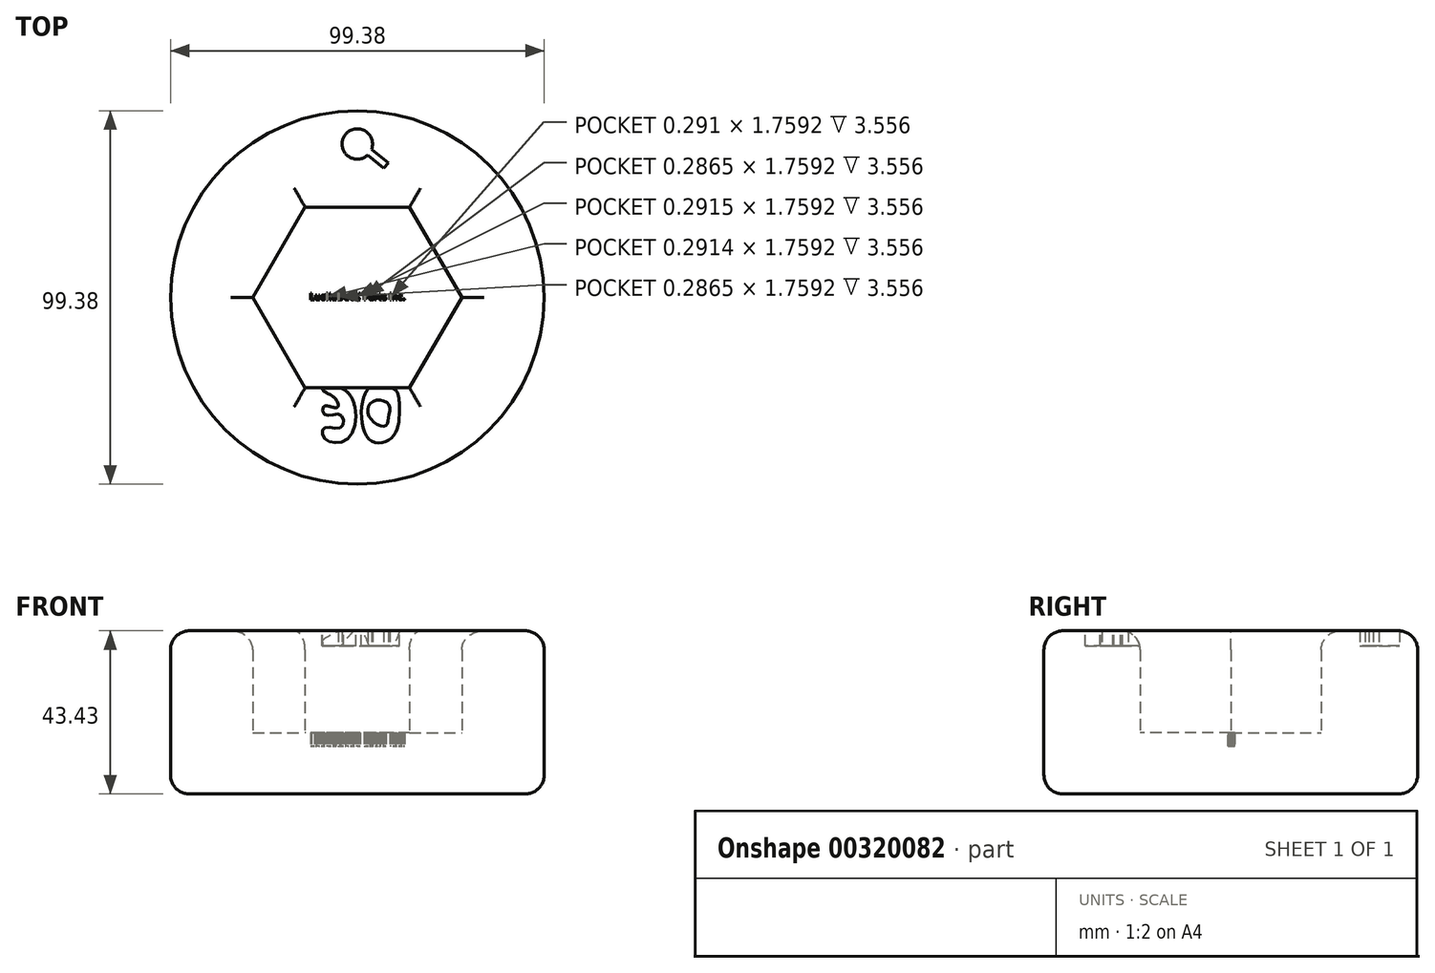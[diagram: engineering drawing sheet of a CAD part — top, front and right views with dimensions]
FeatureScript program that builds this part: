
annotation { "Feature Type Name" : "Feature", "Feature Type Description" : "" }
export const myFeature = defineFeature(function(context is Context, id is Id, definition is map)
    precondition{}
    {
        {
            var Q0;
            Q0=qCreatedBy(makeId("Top.planeOp"),FACE);
            var sketch = newSketch(context, id + "F0", { "sketchPlane" : qUnion([Q0])});
            skCircle(sketch, "E0", {"center": v(0, 0) * mm, "radius": 49.69 * mm});
            skCircle(sketch, "E1.cCircle", {"center": v(0, 0) * mm, "radius": 24.06 * mm, "construction": true});
            skLineSegment(sketch, "E1.0", {"start": v(-13.9, 24.06) * mm, "end": v(13.9, 24.06) * mm});
            skLineSegment(sketch, "E1.1", {"start": v(13.9, 24.06) * mm, "end": v(27.78, 0) * mm});
            skLineSegment(sketch, "E1.2", {"start": v(27.78, 0) * mm, "end": v(13.9, -24.06) * mm});
            skLineSegment(sketch, "E1.3", {"start": v(13.9, -24.06) * mm, "end": v(-13.9, -24.06) * mm});
            skLineSegment(sketch, "E1.4", {"start": v(-13.9, -24.06) * mm, "end": v(-27.78, 0) * mm});
            skLineSegment(sketch, "E1.5", {"start": v(-27.78, 0) * mm, "end": v(-13.9, 24.06) * mm});
            skPoint(sketch, "E1.0.midPoint", {"position": v(0, 24.06) * mm});
            skPoint(sketch, "E2.oppositeSnap0", {"position": v(0, -24.06) * mm});
            skSolve(sketch);
        }
        {
            var Q0;
            Q0=makeQuery(id+"F0.imprint","IMPRINT",FACE,{"disambiguationData":[TD([[makeQuery(id+"F0.imprint","IMPRINT",EDGE,{"derivedFrom":sQuery(id+"F0.wireOp",EDGE,"E0")}),1.0]])]});
            extrude(context, id + "F1", {"entities" : qUnion([Q0]), "depth" : 43.43 * mm});
        }
        {
            var Q0;
            Q0=qCreatedBy(makeId("Top.planeOp"),FACE);
            var sketch = newSketch(context, id + "F2", { "sketchPlane" : qUnion([Q0])});
            skCircle(sketch, "E3.cCircle", {"center": v(0, 0) * mm, "radius": 32.73 * mm, "construction": true});
            skLineSegment(sketch, "E3.0", {"start": v(18.9, -32.73) * mm, "end": v(-18.9, -32.73) * mm});
            skLineSegment(sketch, "E3.1", {"start": v(-18.9, -32.73) * mm, "end": v(-37.8, 0) * mm});
            skLineSegment(sketch, "E3.2", {"start": v(-37.8, 0) * mm, "end": v(-18.9, 32.73) * mm});
            skLineSegment(sketch, "E3.3", {"start": v(-18.9, 32.73) * mm, "end": v(18.9, 32.73) * mm});
            skLineSegment(sketch, "E3.4", {"start": v(18.9, 32.73) * mm, "end": v(37.8, 0) * mm});
            skLineSegment(sketch, "E3.5", {"start": v(37.8, 0) * mm, "end": v(18.9, -32.73) * mm});
            skPoint(sketch, "E3.0.midPoint", {"position": v(0, -32.73) * mm});
            skSolve(sketch);
        }
        {
            var Q0;
            Q0 = qSketchRegion(id + "F2", true);
            extrude(context, id + "F3", {"entities" : qUnion([Q0]), "operationType" : NewBodyOperationType.ADD, "depth" : 16.26 * mm});
        }
        {
            var Q0;
            Q0=qCreatedBy(makeId("Top.planeOp"),FACE);
            cPlane(context, id + "F4", {"entities" : qUnion([Q0]), "cplaneType" : CPlaneType.OFFSET, "offset" : 12.7 * mm, "width" : 152.4 * mm, "height" : 152.4 * mm});
        }
        {
            var Q0;
            Q0=qCreatedBy(id+"F4.planeOp",FACE);
            var sketch = newSketch(context, id + "F5", { "sketchPlane" : qUnion([Q0])});
            skText(sketch, "E4", { "text": "LucKaDucK Parts Inc.", "fontName": "AllertaStencil-Regular.ttf"});
            const initialGuessF5  = {"E4": [-0.0127, -0.00066, 1, 0, 0.00176]};
            skSetInitialGuess(sketch, initialGuessF5);
            skSolve(sketch);
        }
        {
            var Q0;
            Q0 = qSketchRegion(id + "F5", true);
            extrude(context, id + "F6", {"entities" : qUnion([Q0]), "operationType" : NewBodyOperationType.REMOVE, "depth" : 4.6 * mm});
        }
        {
            var Q0;
            Q0=qCreatedBy(makeId("Top.planeOp"),FACE);
            cPlane(context, id + "F7", {"entities" : qUnion([Q0]), "cplaneType" : CPlaneType.OFFSET, "offset" : 39.37 * mm, "width" : 152.4 * mm, "height" : 152.4 * mm});
        }
        {
            var Q0;
            Q0=qCreatedBy(id+"F7.planeOp",FACE);
            var sketch = newSketch(context, id + "F8", { "sketchPlane" : qUnion([Q0])});
            skFitSpline(sketch, "E5", {"points": [v(-9.26, -24.46) * mm, v(-3.12, -24.78) * mm, v(-1.98, -37) * mm, v(-8.58, -37.65) * mm, v(-8.8, -34.76) * mm, v(-4.26, -34.44) * mm, v(-4.49, -31.22) * mm, v(-8.58, -31.22) * mm, v(-8.8, -28.97) * mm, v(-5.4, -29.29) * mm, v(-6.08, -26.71) * mm, v(-9.26, -24.46) * mm]});
            skFitSpline(sketch, "E6", {"points": [v(2.8, -24.46) * mm, v(2.8, -37.33) * mm, v(9.16, -37.33) * mm, v(11.2, -29.29) * mm, v(10.3, -24.78) * mm, v(7.8, -23.82) * mm, v(2.8, -24.46) * mm]});
            skFitSpline(sketch, "E7", {"points": [v(5.07, -27.36) * mm, v(2.8, -29.6) * mm, v(4.38, -33.15) * mm, v(7.57, -34.11) * mm, v(8.25, -31.86) * mm, v(8.48, -28.64) * mm, v(5.07, -27.36) * mm]});
            skCircle(sketch, "E8", {"center": v(0, 40.84) * mm, "radius": 4.05 * mm});
            skLineSegment(sketch, "E9", {"start": v(2.79, 37.9) * mm, "end": v(7.06, 34.38) * mm});
            skLineSegment(sketch, "E10", {"start": v(7.06, 34.38) * mm, "end": v(8.21, 35.78) * mm});
            skLineSegment(sketch, "E11", {"start": v(8.21, 35.78) * mm, "end": v(3.8, 39.43) * mm});
            skSolve(sketch);
        }
        {
            var Q0;
            Q0=makeQuery(id+"F8.imprint","IMPRINT",FACE,{"disambiguationData":[TD([[makeQuery(id+"F8.imprint","IMPRINT",EDGE,{"derivedFrom":sQuery(id+"F8.wireOp",EDGE,"E5")}),-1.0]])]});
            extrude(context, id + "F9", {"entities" : qUnion([Q0]), "operationType" : NewBodyOperationType.REMOVE, "depth" : 25.4 * mm});
        }
        {
            var Q0;
            Q0=makeQuery(id+"F8.imprint","IMPRINT",FACE,{"disambiguationData":[TD([[makeQuery(id+"F8.imprint","IMPRINT",EDGE,{"derivedFrom":sQuery(id+"F8.wireOp",EDGE,"E5")}),-1.0]])]});
            var Q1;
            Q1=makeQuery(id+"F8.imprint","IMPRINT",FACE,{"disambiguationData":[TD([[makeQuery(id+"F8.imprint","IMPRINT",EDGE,{"derivedFrom":sQuery(id+"F8.wireOp",EDGE,"E6")}),1.0]])]});
            var Q2;
            {var subQ0=sQuery(id+"F8.wireOp",EDGE,"E8");var subQ1=makeQuery(id+"F8.imprint","INTERSECT",VERTEX,{"derivedFrom":[subQ0,sQuery(id+"F8.wireOp",EDGE,"E9")]});Q2=makeQuery(id+"F8.imprint","IMPRINT",FACE,{"disambiguationData":[TD([[makeQuery(id+"F8.imprint","IMPRINT",EDGE,{"disambiguationData":[TD([[subQ1,-1.0]])],"derivedFrom":subQ0}),1.0]])]});}
            var Q3;
            {var subQ0=sQuery(id+"F8.wireOp",EDGE,"E9");Q3=makeQuery(id+"F8.imprint","IMPRINT",FACE,{"disambiguationData":[TD([[makeQuery(id+"F8.imprint","IMPRINT",EDGE,{"derivedFrom":subQ0}),1.0]])]});}
            extrude(context, id + "F10", {"entities" : qUnion([Q0, Q1, Q2, Q3]), "operationType" : NewBodyOperationType.REMOVE, "depth" : 15 * mm});
        }
        {
            var Q0;
            Q0=makeQuery(id+"F1.opExtrude","CAP_EDGE",EDGE,{"disambiguationData":[OSD([sQuery(id+"F0.wireOp",EDGE,"E0")])],"isStart":false});
            var Q1;
            Q1=makeQuery(id+"F1.opExtrude","CAP_EDGE",EDGE,{"disambiguationData":[OSD([sQuery(id+"F0.wireOp",EDGE,"E0")])],"isStart":true});
            var Q2;
            Q2=makeQuery(id+"F1.opExtrude","CAP_EDGE",EDGE,{"disambiguationData":[OSD([sQuery(id+"F0.wireOp",EDGE,"E1.2")])],"isStart":false});
            var Q3;
            Q3=makeQuery(id+"F1.opExtrude","CAP_EDGE",EDGE,{"disambiguationData":[OSD([sQuery(id+"F0.wireOp",EDGE,"E1.1")])],"isStart":false});
            var Q4;
            Q4=makeQuery(id+"F1.opExtrude","CAP_EDGE",EDGE,{"disambiguationData":[OSD([sQuery(id+"F0.wireOp",EDGE,"E1.0")])],"isStart":false});
            var Q5;
            Q5=makeQuery(id+"F1.opExtrude","CAP_EDGE",EDGE,{"disambiguationData":[OSD([sQuery(id+"F0.wireOp",EDGE,"E1.5")])],"isStart":false});
            var Q6;
            Q6=makeQuery(id+"F1.opExtrude","CAP_EDGE",EDGE,{"disambiguationData":[OSD([sQuery(id+"F0.wireOp",EDGE,"E1.4")])],"isStart":false});
            var Q7;
            {var subQ0=sQuery(id+"F0.wireOp",EDGE,"E1.3");var subQ1=sQuery(id+"F0.wireOp",EDGE,"E1.2");var subQ3=makeQuery(id+"F1.opExtrude","SWEPT_FACE",FACE,{"disambiguationData":[OSD([subQ1])]});Q7=makeQuery(id+"F10.boolean.opBoolean","SPLIT",EDGE,{"disambiguationData":[TD([subQ3])],"derivedFrom":makeQuery(id+"F9.boolean.opBoolean","SPLIT",EDGE,{"disambiguationData":[TD([subQ3])],"derivedFrom":makeQuery(id+"F1.opExtrude","CAP_EDGE",EDGE,{"disambiguationData":[OSD([subQ0])],"isStart":false})})});}
            var Q8;
            {var subQ0=sQuery(id+"F0.wireOp",EDGE,"E1.3");var subQ1=sQuery(id+"F0.wireOp",EDGE,"E1.2");var subQ4=makeQuery(id+"F9.opExtrude","SWEPT_FACE",FACE,{"disambiguationData":[OSD([sQuery(id+"F8.wireOp",EDGE,"E5")])]});Q8=makeQuery(id+"F10.boolean.opBoolean","SPLIT",EDGE,{"disambiguationData":[TD([makeQuery(id+"F9.boolean.opBoolean","COPY",FACE,{"derivedFrom":subQ4})])],"derivedFrom":makeQuery(id+"F9.boolean.opBoolean","SPLIT",EDGE,{"disambiguationData":[TD([makeQuery(id+"F1.opExtrude","SWEPT_FACE",FACE,{"disambiguationData":[OSD([subQ1])]})])],"derivedFrom":makeQuery(id+"F1.opExtrude","CAP_EDGE",EDGE,{"disambiguationData":[OSD([subQ0])],"isStart":false})})});}
            var Q9;
            {var subQ0=sQuery(id+"F0.wireOp",EDGE,"E1.4");var subQ1=sQuery(id+"F0.wireOp",EDGE,"E1.3");Q9=makeQuery(id+"F9.boolean.opBoolean","SPLIT",EDGE,{"disambiguationData":[TD([makeQuery(id+"F1.opExtrude","SWEPT_FACE",FACE,{"disambiguationData":[OSD([subQ0])]})])],"derivedFrom":makeQuery(id+"F1.opExtrude","CAP_EDGE",EDGE,{"disambiguationData":[OSD([subQ1])],"isStart":false})});}
            fillet(context, id + "F11", {"entities" : qUnion([Q0, Q1, Q2, Q3, Q4, Q5, Q6, Q7, Q8, Q9]), "radius" : 5.08 * mm, "tangentPropagation" : true, "allowEdgeOverflow" : false});
        }
    });
